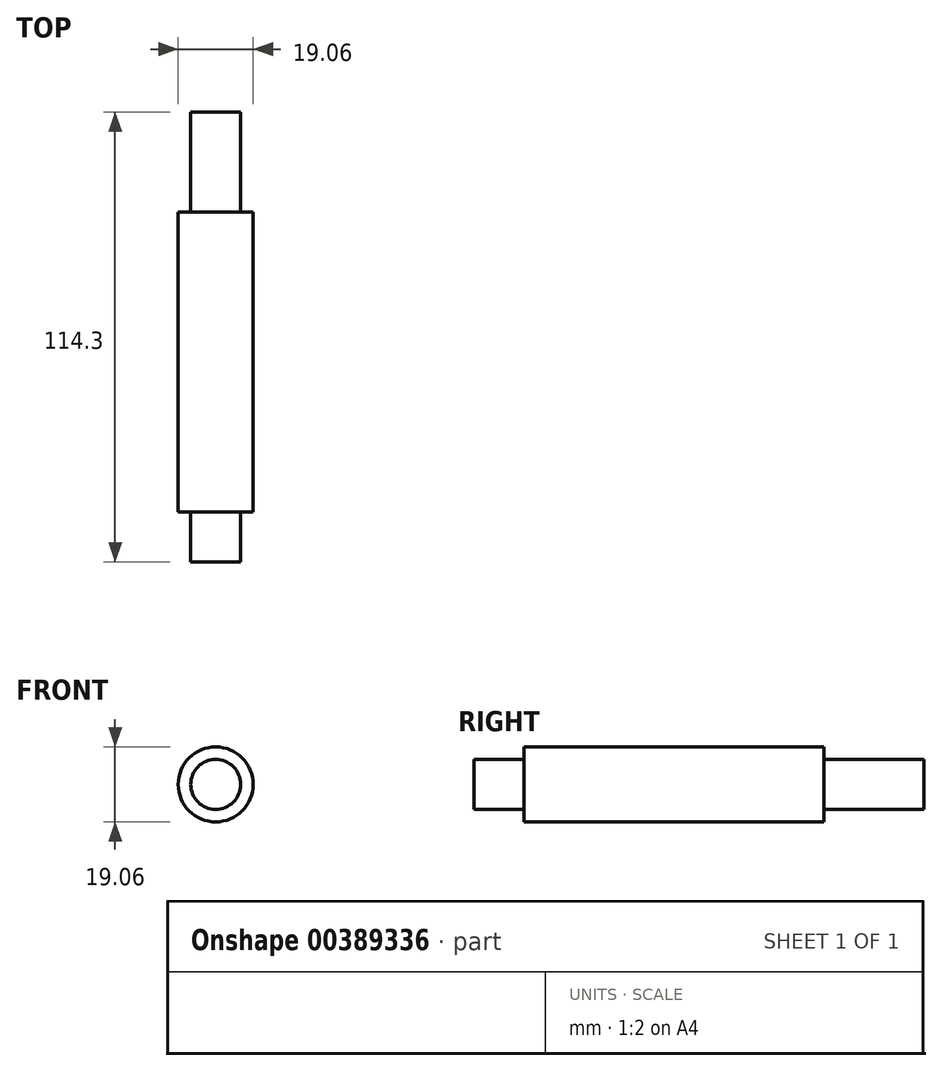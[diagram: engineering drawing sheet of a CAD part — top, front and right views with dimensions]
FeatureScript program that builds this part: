
annotation { "Feature Type Name" : "Feature", "Feature Type Description" : "" }
export const myFeature = defineFeature(function(context is Context, id is Id, definition is map)
    precondition{}
    {
        {
            var Q0;
            Q0=qCreatedBy(makeId("Front.planeOp"),FACE);
            var sketch = newSketch(context, id + "F0", { "sketchPlane" : qUnion([Q0])});
            skCircle(sketch, "E0", {"center": v(0, 0) * mm, "radius": 6.35 * mm});
            skCircle(sketch, "E1", {"center": v(0, 0) * mm, "radius": 9.53 * mm});
            skSolve(sketch);
        }
        {
            var Q0;
            Q0 = qSketchRegion(id + "F0", true);
            var Q1;
            Q1=makeQuery(id+"F0.imprint","IMPRINT",FACE,{"disambiguationData":[TD([[makeQuery(id+"F0.imprint","IMPRINT",EDGE,{"derivedFrom":sQuery(id+"F0.wireOp",EDGE,"E0")}),1.0]])]});
            extrude(context, id + "F1", {"entities" : qUnion([Q0, Q1]), "depth" : 114.3 * mm});
        }
        {
            var Q0;
            Q0=makeQuery(id+"F1.opExtrude","CAP_FACE",FACE,{"disambiguationData":[OSD([sQuery(id+"F0.wireOp",EDGE,"E1")])],"isStart":false});
            var sketch = newSketch(context, id + "F2", { "sketchPlane" : qUnion([Q0])});
            skCircle(sketch, "E2", {"center": v(0, 0) * mm, "radius": 6.35 * mm});
            skSolve(sketch);
        }
        {
            var Q0;
            Q0=makeQuery(id+"F2.imprint","IMPRINT",FACE,{"disambiguationData":[TD([[makeQuery(id+"F2.imprint","IMPRINT",EDGE,{"derivedFrom":sQuery(id+"F2.wireOp",EDGE,"E2")}),-1.0]])]});
            extrude(context, id + "F3", {"entities" : qUnion([Q0]), "operationType" : NewBodyOperationType.REMOVE, "oppositeDirection" : true, "depth" : 12.7 * mm});
        }
        {
            var Q0;
            Q0=makeQuery(id+"F1.opExtrude","CAP_FACE",FACE,{"disambiguationData":[OSD([sQuery(id+"F0.wireOp",EDGE,"E1")])],"isStart":true});
            var sketch = newSketch(context, id + "F4", { "sketchPlane" : qUnion([Q0])});
            skCircle(sketch, "E3", {"center": v(0, 0) * mm, "radius": 6.35 * mm});
            skSolve(sketch);
        }
        {
            var Q0;
            Q0=makeQuery(id+"F4.imprint","IMPRINT",FACE,{"disambiguationData":[TD([[makeQuery(id+"F4.imprint","IMPRINT",EDGE,{"derivedFrom":sQuery(id+"F4.wireOp",EDGE,"E3")}),-1.0]])]});
            extrude(context, id + "F5", {"entities" : qUnion([Q0]), "operationType" : NewBodyOperationType.REMOVE, "oppositeDirection" : true, "depth" : 25.4 * mm});
        }
    });
